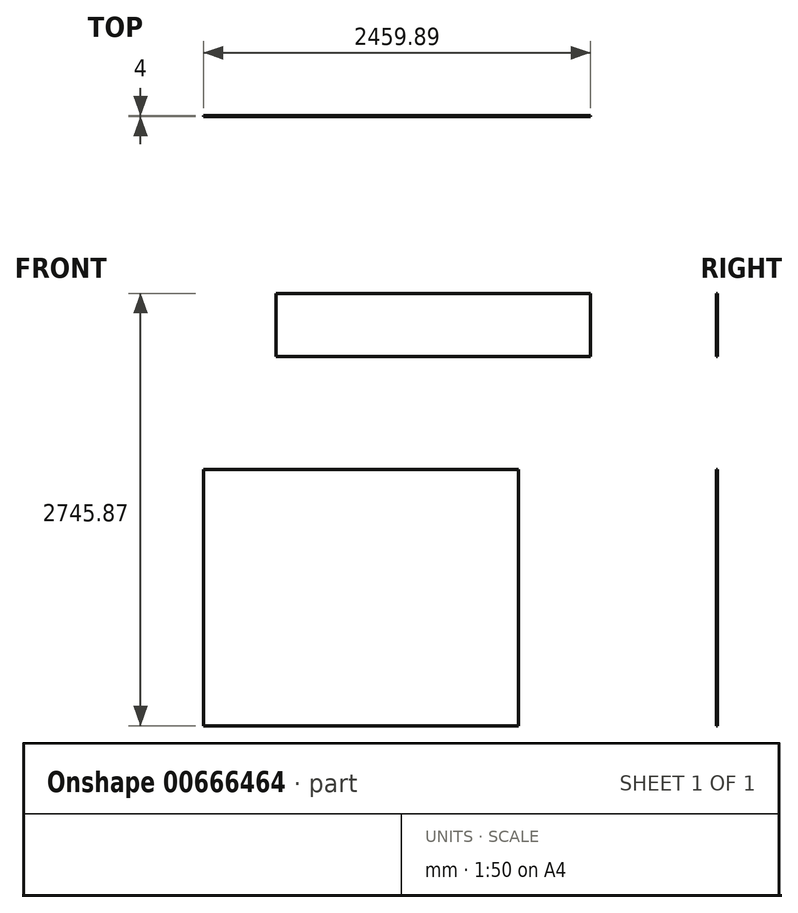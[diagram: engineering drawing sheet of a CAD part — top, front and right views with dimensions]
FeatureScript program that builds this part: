
annotation { "Feature Type Name" : "Feature", "Feature Type Description" : "" }
export const myFeature = defineFeature(function(context is Context, id is Id, definition is map)
    precondition{}
    {
        {
            var Q0;
            Q0=qCreatedBy(makeId("Front.planeOp"),FACE);
            var sketch = newSketch(context, id + "F0", { "sketchPlane" : qUnion([Q0])});
            skLineSegment(sketch, "E0.bottom", {"start": v(-758.74, 1311.94) * mm, "end": v(1241.26, 1311.94) * mm});
            skLineSegment(sketch, "E0.top", {"start": v(-758.74, 911.94) * mm, "end": v(1241.26, 911.94) * mm});
            skLineSegment(sketch, "E0.left", {"start": v(-758.74, 1311.94) * mm, "end": v(-758.74, 911.94) * mm});
            skLineSegment(sketch, "E0.right", {"start": v(1241.26, 1311.94) * mm, "end": v(1241.26, 911.94) * mm});
            skLineSegment(sketch, "E1.bottom", {"start": v(-1218.63, 193.07) * mm, "end": v(781.37, 193.07) * mm});
            skLineSegment(sketch, "E1.top", {"start": v(-1218.63, -1433.93) * mm, "end": v(781.37, -1433.93) * mm});
            skLineSegment(sketch, "E1.left", {"start": v(-1218.63, 193.07) * mm, "end": v(-1218.63, -1433.93) * mm});
            skLineSegment(sketch, "E1.right", {"start": v(781.37, 193.07) * mm, "end": v(781.37, -1433.93) * mm});
            skSolve(sketch);
        }
        {
            var Q0;
            Q0 = qSketchRegion(id + "F0", true);
            extrude(context, id + "F1", {"entities" : qUnion([Q0]), "depth" : 4 * mm, "offsetDistance" : 25 * mm});
        }
    });
